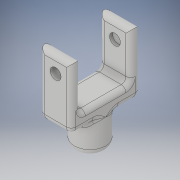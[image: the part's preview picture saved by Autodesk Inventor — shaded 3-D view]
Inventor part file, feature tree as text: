
AUTODESK INVENTOR PART (.ipt)
format: ipt  version: 2019.4 (Build 234330000, 330)  size: 346,624 bytes
history: native  units: mm
features: fillet x5, extrude x4, sketch x4
ambient origin geometry x8: Origin, YZ Plane, XZ Plane, XY Plane, X Axis, Y Axis, Z Axis, Center Point
bodies: Solid1 (feature_tree)
feature tree (13):
  extrude  "Extrusion1"  Depth=10.0mm
  extrude  "Extrusion2"  Depth=10.0mm
  extrude  "Extrusion3"  Depth=10.0mm
  extrude  "Extrusion4"  Depth=1.5mm TaperAngle=0.0deg
  fillet  "Fillet2"  Radius=10.0mm
  fillet  "Fillet4"  Radius=3.0mm
  fillet  "Fillet5"  Radius=10.0mm
  fillet  "Fillet6"  Radius=3.0mm
  fillet  "Fillet7"  Radius=15.0mm
  sketch  "Sketch1"  dims[d0=10.0mm d1=5.0mm]
  sketch  "Sketch2"  dims[d2=10.0mm d3=0.0mm d4=10.0mm]
  sketch  "Sketch3"  dims[d5=15.0mm d6=10.0mm]
  sketch  "Sketch4"  dims[d7=22.0mm d8=5.0mm d9=0.0mm d10=10.0mm d11=3.0mm d12=10.0mm d13=3.0mm d14=15.0mm d15=0.0mm d16=5.0mm d17=3.5mm d18=20.0mm d19=0.0mm d21=2.0mm d23=2.0mm d24=1.5mm d25=1.5mm d26=1.5mm]
